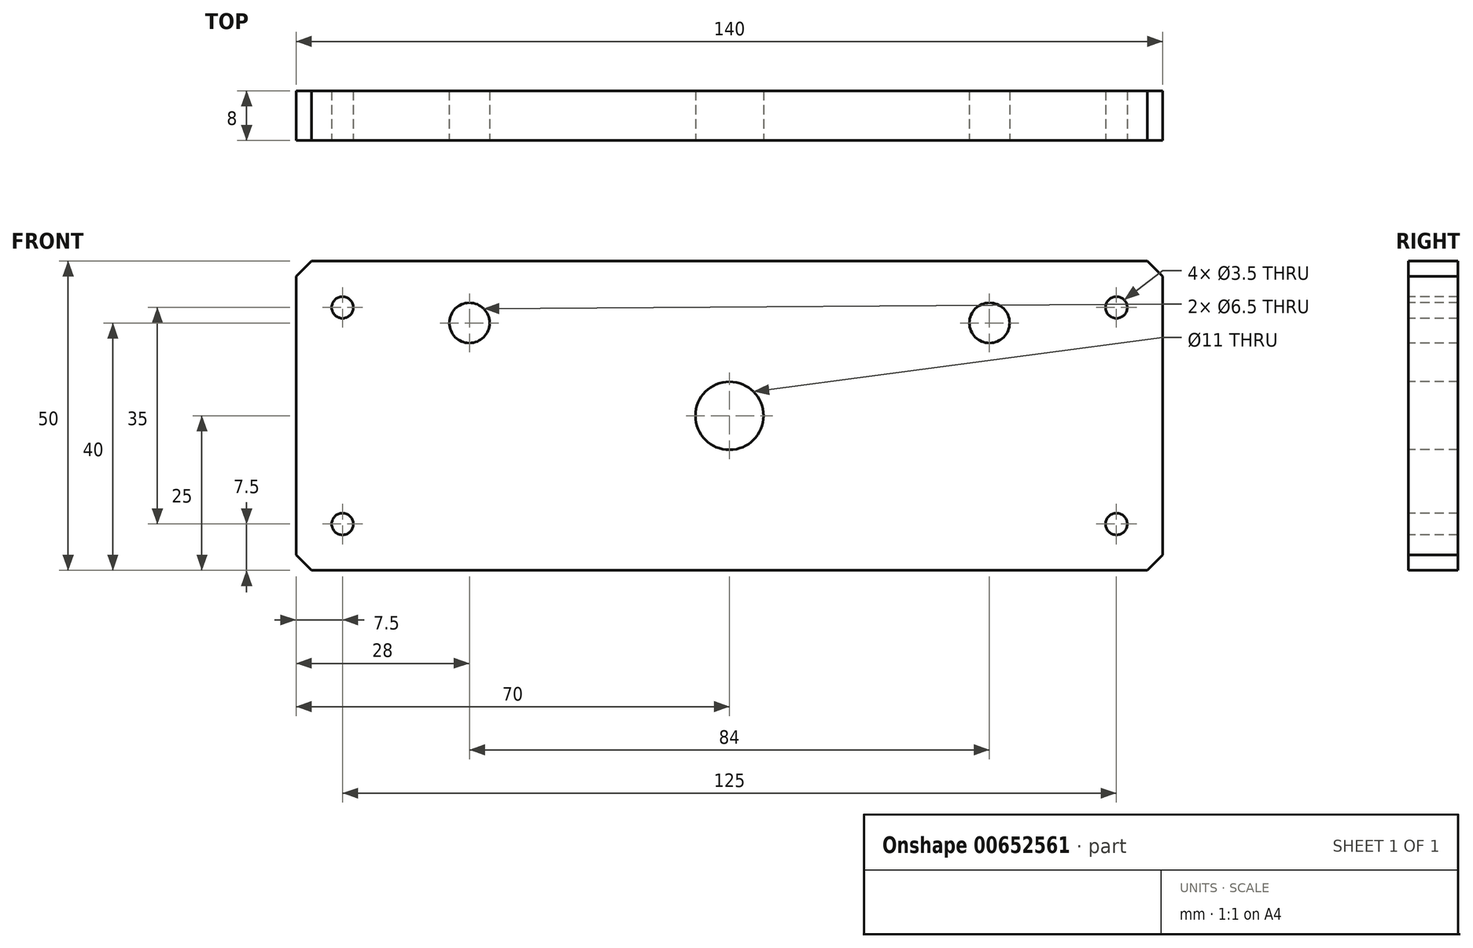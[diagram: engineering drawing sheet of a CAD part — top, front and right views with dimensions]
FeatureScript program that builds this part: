
annotation { "Feature Type Name" : "Feature", "Feature Type Description" : "" }
export const myFeature = defineFeature(function(context is Context, id is Id, definition is map)
    precondition{}
    {
        {
            var Q0;
            Q0=qCreatedBy(makeId("Front.planeOp"),FACE);
            var sketch = newSketch(context, id + "F0", { "sketchPlane" : qUnion([Q0])});
            skLineSegment(sketch, "E0.bottom", {"start": v(70, 25) * mm, "end": v(-70, 25) * mm});
            skLineSegment(sketch, "E0.top", {"start": v(70, -25) * mm, "end": v(-70, -25) * mm});
            skLineSegment(sketch, "E0.left", {"start": v(70, 25) * mm, "end": v(70, -25) * mm});
            skLineSegment(sketch, "E0.right", {"start": v(-70, 25) * mm, "end": v(-70, -25) * mm});
            skPoint(sketch, "E0.middle", {"position": v(0, 0) * mm});
            skSolve(sketch);
        }
        {
            var Q0;
            Q0 = qSketchRegion(id + "F0", true);
            extrude(context, id + "F1", {"entities" : qUnion([Q0]), "depth" : 8 * mm, "offsetDistance" : 25 * mm});
        }
        {
            var Q0;
            Q0=makeQuery(id+"F1.opExtrude","SWEPT_EDGE",EDGE,{"disambiguationData":[OSD([sQuery(id+"F0.wireOp",EDGE,"E0.bottom"),sQuery(id+"F0.wireOp",EDGE,"E0.left")])]});
            var Q1;
            Q1=makeQuery(id+"F1.opExtrude","SWEPT_EDGE",EDGE,{"disambiguationData":[OSD([sQuery(id+"F0.wireOp",EDGE,"E0.bottom"),sQuery(id+"F0.wireOp",EDGE,"E0.right")])]});
            var Q2;
            Q2=makeQuery(id+"F1.opExtrude","SWEPT_EDGE",EDGE,{"disambiguationData":[OSD([sQuery(id+"F0.wireOp",EDGE,"E0.top"),sQuery(id+"F0.wireOp",EDGE,"E0.left")])]});
            var Q3;
            Q3=makeQuery(id+"F1.opExtrude","SWEPT_EDGE",EDGE,{"disambiguationData":[OSD([sQuery(id+"F0.wireOp",EDGE,"E0.top"),sQuery(id+"F0.wireOp",EDGE,"E0.right")])]});
            chamfer(context, id + "F2", {"entities" : qUnion([Q0, Q1, Q2, Q3]), "width" : 2.5 * mm, "tangentPropagation" : true});
        }
        {
            var Q0;
            Q0=makeQuery(id+"F1.opExtrude","CAP_FACE",FACE,{"disambiguationData":[OSD([sQuery(id+"F0.wireOp",EDGE,"E0.bottom"),sQuery(id+"F0.wireOp",EDGE,"E0.top"),sQuery(id+"F0.wireOp",EDGE,"E0.left"),sQuery(id+"F0.wireOp",EDGE,"E0.right")])],"isStart":false});
            var sketch = newSketch(context, id + "F3", { "sketchPlane" : qUnion([Q0])});
            skPoint(sketch, "E1", {"position": v(-62.5, 17.5) * mm});
            skPoint(sketch, "E2", {"position": v(-62.5, -17.5) * mm});
            skPoint(sketch, "E3", {"position": v(62.5, -17.5) * mm});
            skPoint(sketch, "E4", {"position": v(62.5, 17.5) * mm});
            skPoint(sketch, "E5", {"position": v(-42, 15) * mm});
            skPoint(sketch, "E6", {"position": v(42, 15) * mm});
            skPoint(sketch, "E7", {"position": v(0, 0) * mm});
            skSolve(sketch);
        }
        {
            var Q0;
            Q0=sQuery(id+"F3.wireOp",VERTEX,"E4");
            var Q1;
            Q1=sQuery(id+"F3.wireOp",VERTEX,"E3");
            var Q2;
            Q2=sQuery(id+"F3.wireOp",VERTEX,"E2");
            var Q3;
            Q3=sQuery(id+"F3.wireOp",VERTEX,"E1");
            var Q4;
            Q4=makeQuery(id+"F1.opExtrude","SWEPT_BODY",BODY,{"disambiguationData":[OSD([sQuery(id+"F0.wireOp",EDGE,"E0.bottom"),sQuery(id+"F0.wireOp",EDGE,"E0.top"),sQuery(id+"F0.wireOp",EDGE,"E0.left"),sQuery(id+"F0.wireOp",EDGE,"E0.right")])]});
            hole(context, id + "F4", {"style" : HoleStyle.SIMPLE, "endStyle" : HoleEndStyle.THROUGH, "holeDiameter" : 3.5 * mm, "majorDiameter" : 5 * mm, "isTappedThrough" : true, "tappedDepth" : 12 * mm, "tapClearance" : 3, "locations" : qUnion([Q0, Q1, Q2, Q3]), "scope" : qUnion([Q4])});
        }
        {
            var Q0;
            Q0=sQuery(id+"F3.wireOp",VERTEX,"E6");
            var Q1;
            Q1=sQuery(id+"F3.wireOp",VERTEX,"E5");
            var Q2;
            Q2=makeQuery(id+"F1.opExtrude","SWEPT_BODY",BODY,{"disambiguationData":[OSD([sQuery(id+"F0.wireOp",EDGE,"E0.bottom"),sQuery(id+"F0.wireOp",EDGE,"E0.top"),sQuery(id+"F0.wireOp",EDGE,"E0.left"),sQuery(id+"F0.wireOp",EDGE,"E0.right")])]});
            hole(context, id + "F5", {"style" : HoleStyle.SIMPLE, "endStyle" : HoleEndStyle.THROUGH, "holeDiameter" : 6.5 * mm, "majorDiameter" : 5 * mm, "isTappedThrough" : true, "tappedDepth" : 12 * mm, "tapClearance" : 3, "locations" : qUnion([Q0, Q1]), "scope" : qUnion([Q2])});
        }
        {
            var Q0;
            Q0=sQuery(id+"F3.wireOp",VERTEX,"E7");
            var Q1;
            Q1=makeQuery(id+"F1.opExtrude","SWEPT_BODY",BODY,{"disambiguationData":[OSD([sQuery(id+"F0.wireOp",EDGE,"E0.bottom"),sQuery(id+"F0.wireOp",EDGE,"E0.top"),sQuery(id+"F0.wireOp",EDGE,"E0.left"),sQuery(id+"F0.wireOp",EDGE,"E0.right")])]});
            hole(context, id + "F6", {"style" : HoleStyle.SIMPLE, "endStyle" : HoleEndStyle.THROUGH, "standardTappedOrClearance" : lookupTablePath({ "standard" : "ISO", "fit" : "Normal", "size" : "M10", "type" : "Clearance" }), "standardBlindInLast" : lookupTablePath({ "fit" : "Standard", "standard" : "ISO", "size" : "M10", "type" : "Clearance" }), "holeDiameter" : 11 * mm, "majorDiameter" : 5 * mm, "isTappedThrough" : true, "tappedDepth" : 12 * mm, "tapClearance" : 3, "locations" : qUnion([Q0]), "scope" : qUnion([Q1])});
        }
    });
